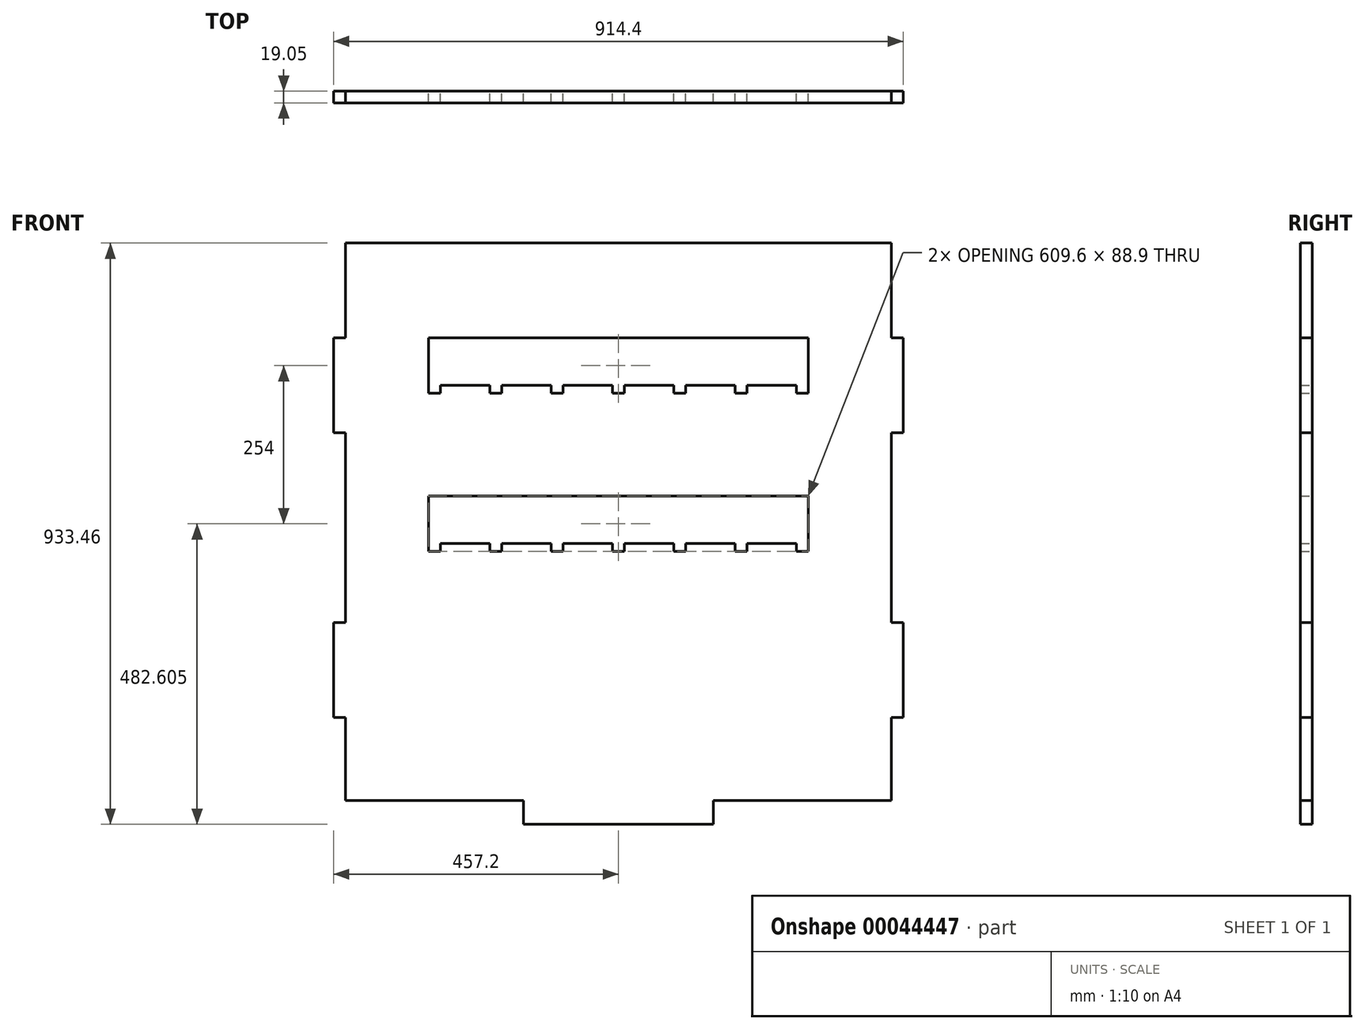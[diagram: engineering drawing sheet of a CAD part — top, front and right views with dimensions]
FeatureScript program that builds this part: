
annotation { "Feature Type Name" : "Feature", "Feature Type Description" : "" }
export const myFeature = defineFeature(function(context is Context, id is Id, definition is map)
    precondition{}
    {
        {
            var Q0;
            Q0=qCreatedBy(makeId("Front.planeOp"),FACE);
            var sketch = newSketch(context, id + "F0", { "sketchPlane" : qUnion([Q0])});
            skLineSegment(sketch, "E0.rect.bottom", {"start": v(-438.15, -447.68) * mm, "end": v(438.15, -447.68) * mm});
            skLineSegment(sketch, "E0.rect.top", {"start": v(-438.15, 447.68) * mm, "end": v(438.15, 447.68) * mm});
            skLineSegment(sketch, "E0.rect.left", {"start": v(-438.15, -447.68) * mm, "end": v(-438.15, 447.68) * mm});
            skLineSegment(sketch, "E0.rect.right", {"start": v(438.15, -447.68) * mm, "end": v(438.15, 447.68) * mm});
            skPoint(sketch, "E0.rect.middle", {"position": v(0, 0) * mm});
            skLineSegment(sketch, "E1.bottom", {"start": v(-438.15, 295.28) * mm, "end": v(-457.2, 295.28) * mm});
            skLineSegment(sketch, "E1.top", {"start": v(-438.15, 142.87) * mm, "end": v(-457.2, 142.87) * mm});
            skLineSegment(sketch, "E1.left", {"start": v(-438.15, 295.28) * mm, "end": v(-438.15, 142.87) * mm});
            skLineSegment(sketch, "E1.right", {"start": v(-457.2, 295.28) * mm, "end": v(-457.2, 142.87) * mm});
            skLineSegment(sketch, "E2.bottom", {"start": v(-438.15, -161.92) * mm, "end": v(-457.2, -161.92) * mm});
            skLineSegment(sketch, "E2.top", {"start": v(-438.15, -314.32) * mm, "end": v(-457.2, -314.32) * mm});
            skLineSegment(sketch, "E2.left", {"start": v(-438.15, -161.92) * mm, "end": v(-438.15, -314.32) * mm});
            skLineSegment(sketch, "E2.right", {"start": v(-457.2, -161.92) * mm, "end": v(-457.2, -314.32) * mm});
            skLineSegment(sketch, "E3.bottom", {"start": v(-152.4, -447.67) * mm, "end": v(152.4, -447.67) * mm});
            skLineSegment(sketch, "E3.top", {"start": v(-152.4, -485.78) * mm, "end": v(152.4, -485.77) * mm});
            skLineSegment(sketch, "E3.left", {"start": v(-152.4, -447.68) * mm, "end": v(-152.4, -485.78) * mm});
            skLineSegment(sketch, "E3.right", {"start": v(152.4, -447.67) * mm, "end": v(152.4, -485.77) * mm});
            skLineSegment(sketch, "E4.MirrorCS", {"start": v(438.15, -314.32) * mm, "end": v(457.2, -314.32) * mm});
            skLineSegment(sketch, "E5.MirrorCS", {"start": v(438.15, 142.88) * mm, "end": v(457.2, 142.88) * mm});
            skLineSegment(sketch, "E6.MirrorCS", {"start": v(438.15, -161.92) * mm, "end": v(457.2, -161.92) * mm});
            skLineSegment(sketch, "E7.MirrorCS", {"start": v(438.15, 295.28) * mm, "end": v(457.2, 295.28) * mm});
            skLineSegment(sketch, "E8.MirrorCS", {"start": v(-152.4, -447.67) * mm, "end": v(-152.4, -485.77) * mm});
            skLineSegment(sketch, "E9.MirrorCS", {"start": v(152.4, -447.68) * mm, "end": v(152.4, -485.78) * mm});
            skLineSegment(sketch, "E10.MirrorCS", {"start": v(152.4, -447.67) * mm, "end": v(-152.4, -447.68) * mm});
            skLineSegment(sketch, "E11.MirrorCS", {"start": v(457.2, -161.92) * mm, "end": v(457.2, -314.32) * mm});
            skLineSegment(sketch, "E12.MirrorCS", {"start": v(438.15, -161.92) * mm, "end": v(438.15, -314.32) * mm});
            skLineSegment(sketch, "E13.MirrorCS", {"start": v(438.15, 295.28) * mm, "end": v(438.15, 142.87) * mm});
            skLineSegment(sketch, "E14.MirrorCS", {"start": v(152.4, -485.78) * mm, "end": v(-152.4, -485.78) * mm});
            skLineSegment(sketch, "E15.MirrorCS", {"start": v(457.2, 295.28) * mm, "end": v(457.2, 142.87) * mm});
            skLineSegment(sketch, "E16.bottom", {"start": v(-304.8, -34.92) * mm, "end": v(304.8, -34.92) * mm});
            skLineSegment(sketch, "E16.top", {"start": v(-304.8, 41.28) * mm, "end": v(304.8, 41.28) * mm});
            skLineSegment(sketch, "E16.left", {"start": v(-304.8, -34.92) * mm, "end": v(-304.8, 41.28) * mm});
            skLineSegment(sketch, "E16.right", {"start": v(304.8, -34.92) * mm, "end": v(304.8, 41.28) * mm});
            skLineSegment(sketch, "E17.top", {"start": v(304.8, 295.27) * mm, "end": v(-304.8, 295.27) * mm});
            skLineSegment(sketch, "E17.left", {"start": v(304.8, 219.08) * mm, "end": v(304.8, 295.27) * mm});
            skLineSegment(sketch, "E17.right", {"start": v(-304.8, 219.07) * mm, "end": v(-304.8, 295.27) * mm});
            skLineSegment(sketch, "E18.bottom", {"start": v(-206.38, 219.07) * mm, "end": v(-187.33, 219.07) * mm});
            skLineSegment(sketch, "E18.top", {"start": v(-206.38, 206.37) * mm, "end": v(-187.33, 206.37) * mm});
            skLineSegment(sketch, "E18.left", {"start": v(-206.38, 219.07) * mm, "end": v(-206.38, 206.38) * mm});
            skLineSegment(sketch, "E18.right", {"start": v(-187.33, 219.07) * mm, "end": v(-187.33, 206.38) * mm});
            skLineSegment(sketch, "E19.bottom", {"start": v(-107.95, 219.07) * mm, "end": v(-88.9, 219.07) * mm});
            skLineSegment(sketch, "E19.top", {"start": v(-107.95, 206.37) * mm, "end": v(-88.9, 206.37) * mm});
            skLineSegment(sketch, "E19.left", {"start": v(-107.95, 219.07) * mm, "end": v(-107.95, 206.38) * mm});
            skLineSegment(sketch, "E19.right", {"start": v(-88.9, 219.07) * mm, "end": v(-88.9, 206.38) * mm});
            skLineSegment(sketch, "E20.bottom", {"start": v(-9.53, 219.07) * mm, "end": v(9.52, 219.07) * mm});
            skLineSegment(sketch, "E20.top", {"start": v(-9.53, 206.37) * mm, "end": v(9.52, 206.37) * mm});
            skLineSegment(sketch, "E20.left", {"start": v(-9.53, 219.08) * mm, "end": v(-9.53, 206.38) * mm});
            skLineSegment(sketch, "E20.right", {"start": v(9.52, 219.08) * mm, "end": v(9.52, 206.38) * mm});
            skLineSegment(sketch, "E21.bottom", {"start": v(88.9, 219.07) * mm, "end": v(107.95, 219.07) * mm});
            skLineSegment(sketch, "E21.top", {"start": v(88.9, 206.38) * mm, "end": v(107.95, 206.38) * mm});
            skLineSegment(sketch, "E21.left", {"start": v(88.9, 219.08) * mm, "end": v(88.9, 206.38) * mm});
            skLineSegment(sketch, "E21.right", {"start": v(107.95, 219.08) * mm, "end": v(107.95, 206.38) * mm});
            skLineSegment(sketch, "E22.bottom", {"start": v(187.32, 219.07) * mm, "end": v(206.37, 219.08) * mm});
            skLineSegment(sketch, "E22.top", {"start": v(187.32, 206.38) * mm, "end": v(206.37, 206.38) * mm});
            skLineSegment(sketch, "E22.left", {"start": v(187.32, 219.08) * mm, "end": v(187.32, 206.38) * mm});
            skLineSegment(sketch, "E22.right", {"start": v(206.37, 219.08) * mm, "end": v(206.37, 206.38) * mm});
            skLineSegment(sketch, "E23.right", {"start": v(-187.32, -34.92) * mm, "end": v(-187.32, -47.62) * mm});
            skLineSegment(sketch, "E23.left", {"start": v(-206.38, -34.92) * mm, "end": v(-206.38, -47.62) * mm});
            skLineSegment(sketch, "E23.bottom", {"start": v(-206.37, -34.92) * mm, "end": v(-187.32, -34.92) * mm});
            skLineSegment(sketch, "E23.top", {"start": v(-206.38, -47.62) * mm, "end": v(-187.32, -47.62) * mm});
            skLineSegment(sketch, "E24.bottom", {"start": v(-107.95, -34.92) * mm, "end": v(-88.9, -34.92) * mm});
            skLineSegment(sketch, "E24.top", {"start": v(-107.95, -47.62) * mm, "end": v(-88.9, -47.62) * mm});
            skLineSegment(sketch, "E24.left", {"start": v(-107.95, -34.92) * mm, "end": v(-107.95, -47.62) * mm});
            skLineSegment(sketch, "E24.right", {"start": v(-88.9, -34.92) * mm, "end": v(-88.9, -47.62) * mm});
            skLineSegment(sketch, "E25.bottom", {"start": v(-9.53, -34.92) * mm, "end": v(9.53, -34.92) * mm});
            skLineSegment(sketch, "E25.top", {"start": v(-9.52, -47.62) * mm, "end": v(9.53, -47.62) * mm});
            skLineSegment(sketch, "E25.left", {"start": v(-9.52, -34.92) * mm, "end": v(-9.52, -47.62) * mm});
            skLineSegment(sketch, "E25.right", {"start": v(9.53, -34.92) * mm, "end": v(9.53, -47.62) * mm});
            skLineSegment(sketch, "E26.bottom", {"start": v(187.33, -34.92) * mm, "end": v(206.38, -34.92) * mm});
            skLineSegment(sketch, "E26.top", {"start": v(187.33, -47.62) * mm, "end": v(206.38, -47.62) * mm});
            skLineSegment(sketch, "E26.left", {"start": v(187.33, -34.92) * mm, "end": v(187.33, -47.62) * mm});
            skLineSegment(sketch, "E26.right", {"start": v(206.38, -34.92) * mm, "end": v(206.38, -47.62) * mm});
            skLineSegment(sketch, "E27.bottom", {"start": v(88.9, -34.92) * mm, "end": v(107.95, -34.92) * mm});
            skLineSegment(sketch, "E27.top", {"start": v(88.9, -47.62) * mm, "end": v(107.95, -47.62) * mm});
            skLineSegment(sketch, "E27.left", {"start": v(88.9, -34.92) * mm, "end": v(88.9, -47.62) * mm});
            skLineSegment(sketch, "E27.right", {"start": v(107.95, -34.92) * mm, "end": v(107.95, -47.62) * mm});
            skLineSegment(sketch, "E28", {"start": v(-304.8, 219.07) * mm, "end": v(304.8, 219.08) * mm});
            skLineSegment(sketch, "E29.bottom", {"start": v(304.8, 219.08) * mm, "end": v(285.75, 219.08) * mm});
            skLineSegment(sketch, "E29.top", {"start": v(304.8, 206.38) * mm, "end": v(285.75, 206.38) * mm});
            skLineSegment(sketch, "E29.left", {"start": v(304.8, 219.08) * mm, "end": v(304.8, 206.38) * mm});
            skLineSegment(sketch, "E29.right", {"start": v(285.75, 219.08) * mm, "end": v(285.75, 206.38) * mm});
            skLineSegment(sketch, "E30.bottom", {"start": v(-304.8, 219.07) * mm, "end": v(-285.75, 219.07) * mm});
            skLineSegment(sketch, "E30.top", {"start": v(-304.8, 206.37) * mm, "end": v(-285.75, 206.37) * mm});
            skLineSegment(sketch, "E30.left", {"start": v(-304.8, 219.07) * mm, "end": v(-304.8, 206.37) * mm});
            skLineSegment(sketch, "E30.right", {"start": v(-285.75, 219.07) * mm, "end": v(-285.75, 206.37) * mm});
            skLineSegment(sketch, "E31.bottom", {"start": v(304.8, -34.92) * mm, "end": v(285.75, -34.92) * mm});
            skLineSegment(sketch, "E31.top", {"start": v(304.8, -47.62) * mm, "end": v(285.75, -47.62) * mm});
            skLineSegment(sketch, "E31.left", {"start": v(304.8, -34.92) * mm, "end": v(304.8, -47.62) * mm});
            skLineSegment(sketch, "E31.right", {"start": v(285.75, -34.92) * mm, "end": v(285.75, -47.62) * mm});
            skLineSegment(sketch, "E32.bottom", {"start": v(-304.8, -34.92) * mm, "end": v(-285.75, -34.92) * mm});
            skLineSegment(sketch, "E32.top", {"start": v(-304.8, -47.62) * mm, "end": v(-285.75, -47.62) * mm});
            skLineSegment(sketch, "E32.left", {"start": v(-304.8, -34.92) * mm, "end": v(-304.8, -47.62) * mm});
            skLineSegment(sketch, "E32.right", {"start": v(-285.75, -34.92) * mm, "end": v(-285.75, -47.62) * mm});
            skSolve(sketch);
        }
        {
            var Q0;
            {var subQ2=sQuery(id+"F0.wireOp",EDGE,"E0.rect.top");Q0=makeQuery(id+"F0.imprint","IMPRINT",FACE,{"disambiguationData":[TD([[makeQuery(id+"F0.imprint","IMPRINT",EDGE,{"derivedFrom":subQ2}),-1.0]])]});}
            var Q1;
            Q1=makeQuery(id+"F0.imprint","IMPRINT",FACE,{"disambiguationData":[TD([[makeQuery(id+"F0.imprint","IMPRINT",EDGE,{"derivedFrom":sQuery(id+"F0.wireOp",EDGE,"E1.bottom")}),1.0]])]});
            var Q2;
            Q2=makeQuery(id+"F0.imprint","IMPRINT",FACE,{"disambiguationData":[TD([[makeQuery(id+"F0.imprint","IMPRINT",EDGE,{"derivedFrom":sQuery(id+"F0.wireOp",EDGE,"E2.bottom")}),1.0]])]});
            var Q3;
            Q3=makeQuery(id+"F0.imprint","IMPRINT",FACE,{"disambiguationData":[TD([[makeQuery(id+"F0.imprint","IMPRINT",EDGE,{"derivedFrom":sQuery(id+"F0.wireOp",EDGE,"E3.bottom")}),-1.0]])]});
            var Q4;
            Q4=makeQuery(id+"F0.imprint","IMPRINT",FACE,{"disambiguationData":[TD([[makeQuery(id+"F0.imprint","IMPRINT",EDGE,{"derivedFrom":sQuery(id+"F0.wireOp",EDGE,"E8.MirrorCS")}),1.0]])]});
            var Q5;
            Q5=makeQuery(id+"F0.imprint","IMPRINT",FACE,{"disambiguationData":[TD([[makeQuery(id+"F0.imprint","IMPRINT",EDGE,{"derivedFrom":sQuery(id+"F0.wireOp",EDGE,"E5.MirrorCS")}),1.0]])]});
            var Q6;
            {var subQ2=sQuery(id+"F0.wireOp",EDGE,"E4.MirrorCS");Q6=makeQuery(id+"F0.imprint","IMPRINT",FACE,{"disambiguationData":[TD([[makeQuery(id+"F0.imprint","IMPRINT",EDGE,{"derivedFrom":subQ2}),1.0]])]});}
            extrude(context, id + "F1", {"entities" : qUnion([Q0, Q1, Q2, Q3, Q4, Q5, Q6]), "depth" : 19.05 * mm});
        }
    });
